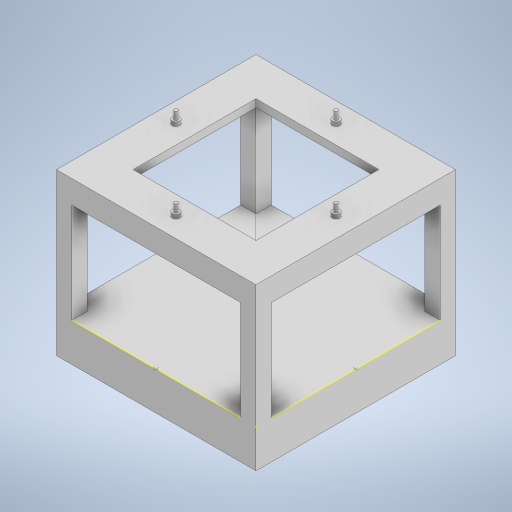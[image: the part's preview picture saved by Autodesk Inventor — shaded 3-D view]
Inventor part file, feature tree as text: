
AUTODESK INVENTOR PART (.ipt)
format: ipt  version: 2023 (Build 270158000, 158)  size: 302,592 bytes
history: native  units: in
note: dims shown in document units (in); Inventor stores cm internally (conversion verified against a paired STEP export)
features: sketch x8, extrude x7, plane x1, other x1, pattern_circular x1
ambient origin geometry x8: Origin, YZ Plane, XZ Plane, XY Plane, X Axis, Y Axis, Z Axis, Center Point
bodies: Solid1 (feature_tree)
feature tree (18):
  extrude  "Extrusion1"  Depth=10.2362in
  sketch  "Sketch2"  dims[d2=7.874in d3=0.0in d4=0.7874in]
  sketch  "Sketch3"  dims[d5=0.7874in d6=0.7874in]
  extrude  "Extrusion2"  Depth=0.7874in
  extrude  "Extrusion3"  Depth=0.7874in
  plane  "Work Plane1"
  extrude  "Extrusion4"  Depth=0.7874in
  extrude  "Extrusion5"  Depth=0.7874in
  extrude  "Extrusion6"  Depth=5.9055in TaperAngle=0.0deg
  extrude  "Extrusion7"  [1 undecoded]
  sketch  "Sketch8"  dims[d21=10.2362in d22=0.0in d23=1.9685in d24=1.9685in d25=1.9685in d26=1.9685in d27=0.3937in d28=0.0in d29=5.1181in d30=5.1181in d31=7.6772in d32=8.7598in d33=8.2185in d34=0.1969in d35=0.5906in d36=0.0in d37=0.3937in d38=0.1969in d39=0.0in d40=1.5748in d41=360.0deg]
  other  "Work Axis2"
  pattern_circular  "Circular Pattern1"  Count=2  [1 undecoded]
  sketch  "Sketch1"  dims[d0=10.2362in d1=10.2362in]
  sketch  "Sketch4"  dims[d7=0.7874in d8=0.7874in]
  sketch  "Sketch5"  dims[d9=0.7874in d10=0.7874in]
  sketch  "Sketch6"  dims[d11=1.9685in d12=5.9055in d13=0.0in]
  sketch  "Sketch7"  dims[d14=10.2362in d15=0.0in d16=-5.1181in d17=0.7874in d18=0.7874in d19=0.7874in d20=1.9685in]
note: 2 required parameter values undecoded (feature->parameter linkage not recoverable at this tier; creation-order binding heuristic only, values carry confidence <= 0.55)
